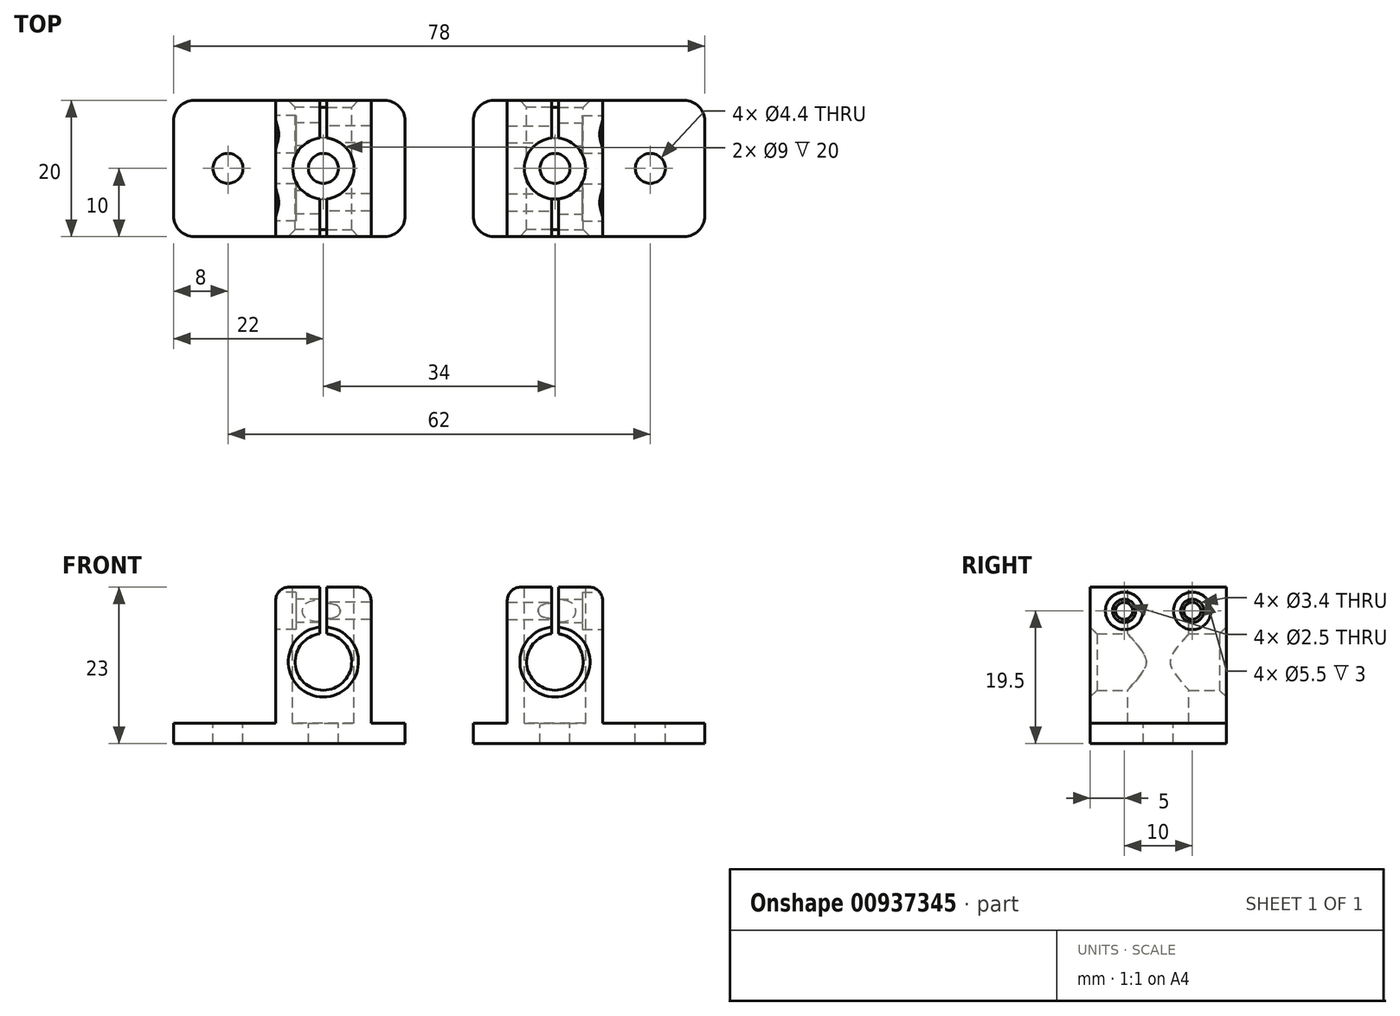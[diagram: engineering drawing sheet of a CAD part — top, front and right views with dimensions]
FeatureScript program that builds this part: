
annotation { "Feature Type Name" : "Feature", "Feature Type Description" : "" }
export const myFeature = defineFeature(function(context is Context, id is Id, definition is map)
    precondition{}
    {
        {
            var Q0;
            Q0=qCreatedBy(makeId("Front.planeOp"),FACE);
            var sketch = newSketch(context, id + "F0", { "sketchPlane" : qUnion([Q0])});
            skLineSegment(sketch, "E0", {"start": v(-22, 0) * mm, "end": v(12, 0) * mm});
            skLineSegment(sketch, "E1", {"start": v(12, 0) * mm, "end": v(12, 3) * mm});
            skLineSegment(sketch, "E2", {"start": v(12, 3) * mm, "end": v(7, 3) * mm});
            skLineSegment(sketch, "E3", {"start": v(7, 3) * mm, "end": v(7, 21) * mm});
            skLineSegment(sketch, "E4", {"start": v(5, 23) * mm, "end": v(0.5, 23) * mm});
            skLineSegment(sketch, "E5", {"start": v(-7, 21) * mm, "end": v(-7, 3) * mm});
            skLineSegment(sketch, "E6", {"start": v(-7, 3) * mm, "end": v(-22, 3) * mm});
            skLineSegment(sketch, "E7", {"start": v(-22, 3) * mm, "end": v(-22, 0) * mm});
            skPoint(sketch, "E8.visualSharp", {"position": v(-7, 23) * mm});
            skArc(sketch, "E8.filletArc", {"start": v(-5, 23) * mm, "mid": v(-6.41, 22.41) * mm, "end": v(-7, 21) * mm});
            skPoint(sketch, "E9.visualSharp", {"position": v(7, 23) * mm});
            skArc(sketch, "E9.filletArc", {"start": v(7, 21) * mm, "mid": v(6.41, 22.41) * mm, "end": v(5, 23) * mm});
            skArc(sketch, "E10", {"start": v(-0.5, 16.12) * mm, "mid": v(0, 7.85) * mm, "end": v(0.5, 16.12) * mm});
            skLineSegment(sketch, "E11", {"start": v(-24.95, 12) * mm, "end": v(15.5, 12) * mm, "construction": true});
            skPoint(sketch, "E11.startSnap0", {"position": v(-7, 12) * mm});
            skLineSegment(sketch, "E12", {"start": v(0, 35.9) * mm, "end": v(0, -4.92) * mm, "construction": true});
            skPoint(sketch, "E12.startSnap0", {"position": v(0, 23) * mm});
            skLineSegment(sketch, "E13", {"start": v(-0.5, 23) * mm, "end": v(-0.5, 16.12) * mm});
            skLineSegment(sketch, "E14", {"start": v(0.5, 23) * mm, "end": v(0.5, 16.12) * mm});
            skLineSegment(sketch, "E15.trimOffspring", {"start": v(-0.5, 23) * mm, "end": v(-5, 23) * mm});
            skSolve(sketch);
        }
        {
            var Q0;
            Q0=makeQuery(id+"F0.imprint","IMPRINT",FACE,{"disambiguationData":[TD([[makeQuery(id+"F0.imprint","IMPRINT",EDGE,{"derivedFrom":sQuery(id+"F0.wireOp",EDGE,"E0")}),1.0]])]});
            extrude(context, id + "F1", {"entities" : qUnion([Q0]), "depth" : 20 * mm, "offsetDistance" : 25 * mm, "symmetric" : true});
        }
        {
            var Q0;
            Q0=makeQuery(id+"F1.opExtrude","CAP_EDGE",EDGE,{"disambiguationData":[OSD([sQuery(id+"F0.wireOp",EDGE,"E10")])],"isStart":false});
            var Q1;
            Q1=makeQuery(id+"F1.opExtrude","CAP_EDGE",EDGE,{"disambiguationData":[OSD([sQuery(id+"F0.wireOp",EDGE,"E10")])],"isStart":true});
            chamfer(context, id + "F2", {"entities" : qUnion([Q0, Q1]), "width" : 1 * mm, "tangentPropagation" : true});
        }
        {
            var Q0;
            Q0=makeQuery(id+"F1.opExtrude","CAP_EDGE",EDGE,{"disambiguationData":[OSD([sQuery(id+"F0.wireOp",EDGE,"E7")])],"isStart":false});
            var Q1;
            Q1=makeQuery(id+"F1.opExtrude","CAP_EDGE",EDGE,{"disambiguationData":[OSD([sQuery(id+"F0.wireOp",EDGE,"E1")])],"isStart":false});
            var Q2;
            Q2=makeQuery(id+"F1.opExtrude","CAP_EDGE",EDGE,{"disambiguationData":[OSD([sQuery(id+"F0.wireOp",EDGE,"E1")])],"isStart":true});
            var Q3;
            Q3=makeQuery(id+"F1.opExtrude","CAP_EDGE",EDGE,{"disambiguationData":[OSD([sQuery(id+"F0.wireOp",EDGE,"E7")])],"isStart":true});
            fillet(context, id + "F3", {"entities" : qUnion([Q0, Q1, Q2, Q3]), "radius" : 3 * mm, "tangentPropagation" : true, "allowEdgeOverflow" : false});
        }
        {
            var Q0;
            Q0=makeQuery(id+"F1.opExtrude","SWEPT_FACE",FACE,{"disambiguationData":[OSD([sQuery(id+"F0.wireOp",EDGE,"E15.trimOffspring")])]});
            var sketch = newSketch(context, id + "F4", { "sketchPlane" : qUnion([Q0])});
            skLineSegment(sketch, "E16", {"start": v(0, -10.74) * mm, "end": v(0, 13.35) * mm, "construction": true});
            skLineSegment(sketch, "E17", {"start": v(39.88, 0) * mm, "end": v(54, 0) * mm, "construction": true});
            skPoint(sketch, "E17.startSnap0", {"position": v(-5, 0) * mm});
            skCircle(sketch, "E18", {"center": v(0, 0) * mm, "radius": 4.5 * mm});
            skSolve(sketch);
        }
        {
            var Q0;
            {var subQ0=sQuery(id+"F4.wireOp",EDGE,"E18");var subQ1=makeQuery(id+"F1.opExtrude","SWEPT_EDGE",EDGE,{"disambiguationData":[OSD([sQuery(id+"F0.wireOp",EDGE,"E13"),sQuery(id+"F0.wireOp",EDGE,"E15.trimOffspring")])]});var subQ2=makeQuery(id+"F4.imprint","INTERSECT",VERTEX,{"disambiguationData":[OD(0.0)],"derivedFrom":[subQ1,subQ0]});Q0=makeQuery(id+"F4.imprint","IMPRINT",FACE,{"disambiguationData":[TD([[makeQuery(id+"F4.imprint","IMPRINT",EDGE,{"disambiguationData":[TD([[subQ2,-1.0]])],"derivedFrom":subQ0}),1.0]])]});}
            var Q1;
            {var subQ0=sQuery(id+"F4.wireOp",EDGE,"E18");var subQ1=makeQuery(id+"F1.opExtrude","SWEPT_EDGE",EDGE,{"disambiguationData":[OSD([sQuery(id+"F0.wireOp",EDGE,"E13"),sQuery(id+"F0.wireOp",EDGE,"E15.trimOffspring")])]});var subQ2=makeQuery(id+"F4.imprint","INTERSECT",VERTEX,{"disambiguationData":[OD(0.0)],"derivedFrom":[subQ1,subQ0]});Q1=makeQuery(id+"F4.imprint","IMPRINT",FACE,{"disambiguationData":[TD([[makeQuery(id+"F4.imprint","IMPRINT",EDGE,{"disambiguationData":[TD([[subQ2,1.0]])],"derivedFrom":subQ0}),1.0]])]});}
            var Q2;
            Q2=makeQuery(id+"F1.opExtrude","SWEPT_FACE",FACE,{"disambiguationData":[OSD([sQuery(id+"F0.wireOp",EDGE,"E6")])]});
            extrude(context, id + "F5", {"entities" : qUnion([Q0, Q1]), "operationType" : NewBodyOperationType.REMOVE, "endBound" : BoundingType.UP_TO_SURFACE, "oppositeDirection" : true, "depth" : 25 * mm, "endBoundEntityFace" : qUnion([Q2]), "offsetDistance" : 25 * mm});
        }
        {
            var Q0;
            Q0=makeQuery(id+"F1.opExtrude","SWEPT_FACE",FACE,{"disambiguationData":[OSD([sQuery(id+"F0.wireOp",EDGE,"E6")])]});
            var sketch = newSketch(context, id + "F6", { "sketchPlane" : qUnion([Q0])});
            skLineSegment(sketch, "E19", {"start": v(-22, 0) * mm, "end": v(60.66, 0) * mm, "construction": true});
            skLineSegment(sketch, "E20", {"start": v(-14, -10.75) * mm, "end": v(-14, 12.73) * mm, "construction": true});
            skLineSegment(sketch, "E21", {"start": v(0, -13.4) * mm, "end": v(0, 14.58) * mm, "construction": true});
            skCircle(sketch, "E22", {"center": v(-14, 0) * mm, "radius": 2.2 * mm});
            skCircle(sketch, "E23", {"center": v(0, 0) * mm, "radius": 2.2 * mm});
            skSolve(sketch);
        }
        {
            var Q0;
            Q0=makeQuery(id+"F6.imprint","IMPRINT",FACE,{"disambiguationData":[TD([[makeQuery(id+"F6.imprint","IMPRINT",EDGE,{"derivedFrom":sQuery(id+"F6.wireOp",EDGE,"E22")}),1.0]])]});
            var Q1;
            Q1=makeQuery(id+"F6.imprint","IMPRINT",FACE,{"disambiguationData":[TD([[makeQuery(id+"F6.imprint","IMPRINT",EDGE,{"derivedFrom":sQuery(id+"F6.wireOp",EDGE,"E23")}),1.0]])]});
            extrude(context, id + "F7", {"entities" : qUnion([Q0, Q1]), "operationType" : NewBodyOperationType.REMOVE, "endBound" : BoundingType.THROUGH_ALL, "oppositeDirection" : true, "depth" : 25 * mm, "offsetDistance" : 25 * mm});
        }
        {
            var Q0;
            Q0=makeQuery(id+"F1.opExtrude","SWEPT_FACE",FACE,{"disambiguationData":[OSD([sQuery(id+"F0.wireOp",EDGE,"E5")])]});
            var sketch = newSketch(context, id + "F8", { "sketchPlane" : qUnion([Q0])});
            skLineSegment(sketch, "E24", {"start": v(-15.78, 19.5) * mm, "end": v(15.39, 19.5) * mm, "construction": true});
            skLineSegment(sketch, "E25", {"start": v(-5, 27.71) * mm, "end": v(-5, 4.3) * mm, "construction": true});
            skLineSegment(sketch, "E26", {"start": v(5, 4.3) * mm, "end": v(5, 26.53) * mm, "construction": true});
            skCircle(sketch, "E27", {"center": v(-5, 19.5) * mm, "radius": 1.25 * mm});
            skCircle(sketch, "E28", {"center": v(-5, 19.5) * mm, "radius": 1.7 * mm});
            skCircle(sketch, "E29", {"center": v(-5, 19.5) * mm, "radius": 2.75 * mm});
            skCircle(sketch, "E30", {"center": v(5, 19.5) * mm, "radius": 1.25 * mm});
            skCircle(sketch, "E31", {"center": v(5, 19.5) * mm, "radius": 1.7 * mm});
            skCircle(sketch, "E32", {"center": v(5, 19.5) * mm, "radius": 2.75 * mm});
            skSolve(sketch);
        }
        {
            var Q0;
            Q0=makeQuery(id+"F8.imprint","IMPRINT",FACE,{"disambiguationData":[TD([[makeQuery(id+"F8.imprint","IMPRINT",EDGE,{"derivedFrom":sQuery(id+"F8.wireOp",EDGE,"E27")}),1.0]])]});
            var Q1;
            Q1=makeQuery(id+"F8.imprint","IMPRINT",FACE,{"disambiguationData":[TD([[makeQuery(id+"F8.imprint","IMPRINT",EDGE,{"derivedFrom":sQuery(id+"F8.wireOp",EDGE,"E30")}),1.0]])]});
            extrude(context, id + "F9", {"entities" : qUnion([Q0, Q1]), "operationType" : NewBodyOperationType.REMOVE, "endBound" : BoundingType.THROUGH_ALL, "oppositeDirection" : true, "depth" : 25 * mm, "offsetDistance" : 25 * mm});
        }
        {
            var Q0;
            Q0=makeQuery(id+"F8.imprint","IMPRINT",FACE,{"disambiguationData":[TD([[makeQuery(id+"F8.imprint","IMPRINT",EDGE,{"derivedFrom":sQuery(id+"F8.wireOp",EDGE,"E27")}),-1.0]])]});
            var Q1;
            Q1=makeQuery(id+"F8.imprint","IMPRINT",FACE,{"disambiguationData":[TD([[makeQuery(id+"F8.imprint","IMPRINT",EDGE,{"derivedFrom":sQuery(id+"F8.wireOp",EDGE,"E30")}),-1.0]])]});
            var Q2;
            {var subQ0=sQuery(id+"F8.wireOp",EDGE,"E31");var subQ1=makeQuery(id+"F1.opExtrude","SWEPT_EDGE",EDGE,{"disambiguationData":[OSD([sQuery(id+"F0.wireOp",EDGE,"E5"),sQuery(id+"F0.wireOp",EDGE,"E8.filletArc")])]});var subQ2=makeQuery(id+"F8.imprint","INTERSECT",VERTEX,{"disambiguationData":[OD(0.0)],"derivedFrom":[subQ1,subQ0]});Q2=makeQuery(id+"F8.imprint","IMPRINT",FACE,{"disambiguationData":[TD([[makeQuery(id+"F8.imprint","IMPRINT",EDGE,{"disambiguationData":[TD([[subQ2,-1.0]])],"derivedFrom":subQ0}),1.0]])]});}
            var Q3;
            {var subQ0=sQuery(id+"F8.wireOp",EDGE,"E28");var subQ1=makeQuery(id+"F1.opExtrude","SWEPT_EDGE",EDGE,{"disambiguationData":[OSD([sQuery(id+"F0.wireOp",EDGE,"E5"),sQuery(id+"F0.wireOp",EDGE,"E8.filletArc")])]});var subQ2=makeQuery(id+"F8.imprint","INTERSECT",VERTEX,{"disambiguationData":[OD(0.0)],"derivedFrom":[subQ1,subQ0]});Q3=makeQuery(id+"F8.imprint","IMPRINT",FACE,{"disambiguationData":[TD([[makeQuery(id+"F8.imprint","IMPRINT",EDGE,{"disambiguationData":[TD([[subQ2,1.0]])],"derivedFrom":subQ0}),1.0]])]});}
            extrude(context, id + "F10", {"entities" : qUnion([Q0, Q1, Q2, Q3]), "operationType" : NewBodyOperationType.REMOVE, "endBound" : BoundingType.UP_TO_NEXT, "oppositeDirection" : true, "depth" : 25 * mm, "offsetDistance" : 25 * mm});
        }
        {
            var Q0;
            {var subQ0=sQuery(id+"F8.wireOp",EDGE,"E31");var subQ1=makeQuery(id+"F1.opExtrude","SWEPT_EDGE",EDGE,{"disambiguationData":[OSD([sQuery(id+"F0.wireOp",EDGE,"E5"),sQuery(id+"F0.wireOp",EDGE,"E8.filletArc")])]});var subQ2=makeQuery(id+"F8.imprint","INTERSECT",VERTEX,{"disambiguationData":[OD(0.0)],"derivedFrom":[subQ1,subQ0]});Q0=makeQuery(id+"F8.imprint","IMPRINT",FACE,{"disambiguationData":[TD([[makeQuery(id+"F8.imprint","IMPRINT",EDGE,{"disambiguationData":[TD([[subQ2,1.0]])],"derivedFrom":subQ0}),-1.0]])]});}
            var Q1;
            {var subQ0=sQuery(id+"F8.wireOp",EDGE,"E31");var subQ1=makeQuery(id+"F1.opExtrude","SWEPT_EDGE",EDGE,{"disambiguationData":[OSD([sQuery(id+"F0.wireOp",EDGE,"E5"),sQuery(id+"F0.wireOp",EDGE,"E8.filletArc")])]});var subQ2=makeQuery(id+"F8.imprint","INTERSECT",VERTEX,{"disambiguationData":[OD(0.0)],"derivedFrom":[subQ1,subQ0]});Q1=makeQuery(id+"F8.imprint","IMPRINT",FACE,{"disambiguationData":[TD([[makeQuery(id+"F8.imprint","IMPRINT",EDGE,{"disambiguationData":[TD([[subQ2,-1.0]])],"derivedFrom":subQ0}),-1.0]])]});}
            var Q2;
            {var subQ0=sQuery(id+"F8.wireOp",EDGE,"E28");var subQ1=makeQuery(id+"F1.opExtrude","SWEPT_EDGE",EDGE,{"disambiguationData":[OSD([sQuery(id+"F0.wireOp",EDGE,"E5"),sQuery(id+"F0.wireOp",EDGE,"E8.filletArc")])]});var subQ2=makeQuery(id+"F8.imprint","INTERSECT",VERTEX,{"disambiguationData":[OD(0.0)],"derivedFrom":[subQ1,subQ0]});Q2=makeQuery(id+"F8.imprint","IMPRINT",FACE,{"disambiguationData":[TD([[makeQuery(id+"F8.imprint","IMPRINT",EDGE,{"disambiguationData":[TD([[subQ2,-1.0]])],"derivedFrom":subQ0}),-1.0]])]});}
            var Q3;
            {var subQ0=sQuery(id+"F8.wireOp",EDGE,"E28");var subQ1=makeQuery(id+"F1.opExtrude","SWEPT_EDGE",EDGE,{"disambiguationData":[OSD([sQuery(id+"F0.wireOp",EDGE,"E5"),sQuery(id+"F0.wireOp",EDGE,"E8.filletArc")])]});var subQ2=makeQuery(id+"F8.imprint","INTERSECT",VERTEX,{"disambiguationData":[OD(0.0)],"derivedFrom":[subQ1,subQ0]});Q3=makeQuery(id+"F8.imprint","IMPRINT",FACE,{"disambiguationData":[TD([[makeQuery(id+"F8.imprint","IMPRINT",EDGE,{"disambiguationData":[TD([[subQ2,1.0]])],"derivedFrom":subQ0}),-1.0]])]});}
            var Q4;
            {var subQ0=sQuery(id+"F8.wireOp",EDGE,"E31");var subQ1=makeQuery(id+"F1.opExtrude","SWEPT_EDGE",EDGE,{"disambiguationData":[OSD([sQuery(id+"F0.wireOp",EDGE,"E5"),sQuery(id+"F0.wireOp",EDGE,"E8.filletArc")])]});var subQ2=makeQuery(id+"F8.imprint","INTERSECT",VERTEX,{"disambiguationData":[OD(0.0)],"derivedFrom":[subQ1,subQ0]});Q4=makeQuery(id+"F8.imprint","IMPRINT",FACE,{"disambiguationData":[TD([[makeQuery(id+"F8.imprint","IMPRINT",EDGE,{"disambiguationData":[TD([[subQ2,-1.0]])],"derivedFrom":subQ0}),1.0]])]});}
            var Q5;
            {var subQ0=sQuery(id+"F8.wireOp",EDGE,"E28");var subQ1=makeQuery(id+"F1.opExtrude","SWEPT_EDGE",EDGE,{"disambiguationData":[OSD([sQuery(id+"F0.wireOp",EDGE,"E5"),sQuery(id+"F0.wireOp",EDGE,"E8.filletArc")])]});var subQ2=makeQuery(id+"F8.imprint","INTERSECT",VERTEX,{"disambiguationData":[OD(0.0)],"derivedFrom":[subQ1,subQ0]});Q5=makeQuery(id+"F8.imprint","IMPRINT",FACE,{"disambiguationData":[TD([[makeQuery(id+"F8.imprint","IMPRINT",EDGE,{"disambiguationData":[TD([[subQ2,1.0]])],"derivedFrom":subQ0}),1.0]])]});}
            extrude(context, id + "F11", {"entities" : qUnion([Q0, Q1, Q2, Q3, Q4, Q5]), "operationType" : NewBodyOperationType.REMOVE, "oppositeDirection" : true, "depth" : 3 * mm, "offsetDistance" : 25 * mm});
        }
        {
            var Q0;
            Q0=makeQuery(id+"F1.opExtrude","SWEPT_BODY",BODY,{"disambiguationData":[OSD([sQuery(id+"F0.wireOp",EDGE,"E0"),sQuery(id+"F0.wireOp",EDGE,"E1"),sQuery(id+"F0.wireOp",EDGE,"E2"),sQuery(id+"F0.wireOp",EDGE,"E3"),sQuery(id+"F0.wireOp",EDGE,"E4"),sQuery(id+"F0.wireOp",EDGE,"E5"),sQuery(id+"F0.wireOp",EDGE,"E6"),sQuery(id+"F0.wireOp",EDGE,"E7"),sQuery(id+"F0.wireOp",EDGE,"E8.filletArc"),sQuery(id+"F0.wireOp",EDGE,"E9.filletArc"),sQuery(id+"F0.wireOp",EDGE,"E10"),sQuery(id+"F0.wireOp",EDGE,"E13"),sQuery(id+"F0.wireOp",EDGE,"E14"),sQuery(id+"F0.wireOp",EDGE,"E15.trimOffspring")])]});
            var Q1;
            Q1=makeQuery(id+"F1.opExtrude","SWEPT_FACE",FACE,{"disambiguationData":[OSD([sQuery(id+"F0.wireOp",EDGE,"E1")])]});
            mirror(context, id + "F12", {"entities" : qUnion([Q0]), "mirrorPlane" : qUnion([Q1])});
        }
        {
            var Q0;
            Q0=makeQuery(id+"F12.opPattern","COPY",BODY,{"derivedFrom":makeQuery(id+"F1.opExtrude","SWEPT_BODY",BODY,{"disambiguationData":[OSD([sQuery(id+"F0.wireOp",EDGE,"E0"),sQuery(id+"F0.wireOp",EDGE,"E1"),sQuery(id+"F0.wireOp",EDGE,"E2"),sQuery(id+"F0.wireOp",EDGE,"E3"),sQuery(id+"F0.wireOp",EDGE,"E4"),sQuery(id+"F0.wireOp",EDGE,"E5"),sQuery(id+"F0.wireOp",EDGE,"E6"),sQuery(id+"F0.wireOp",EDGE,"E7"),sQuery(id+"F0.wireOp",EDGE,"E8.filletArc"),sQuery(id+"F0.wireOp",EDGE,"E9.filletArc"),sQuery(id+"F0.wireOp",EDGE,"E10"),sQuery(id+"F0.wireOp",EDGE,"E13"),sQuery(id+"F0.wireOp",EDGE,"E14"),sQuery(id+"F0.wireOp",EDGE,"E15.trimOffspring")])]}),"instanceName":"1"});
            transform(context, id + "F13", {"entities" : qUnion([Q0]), "transformType" : TransformType.TRANSLATION_3D, "dx" : 10 * mm, "dy" : 0 * mm, "dz" : 0 * mm, "makeCopy" : false});
        }
    });
